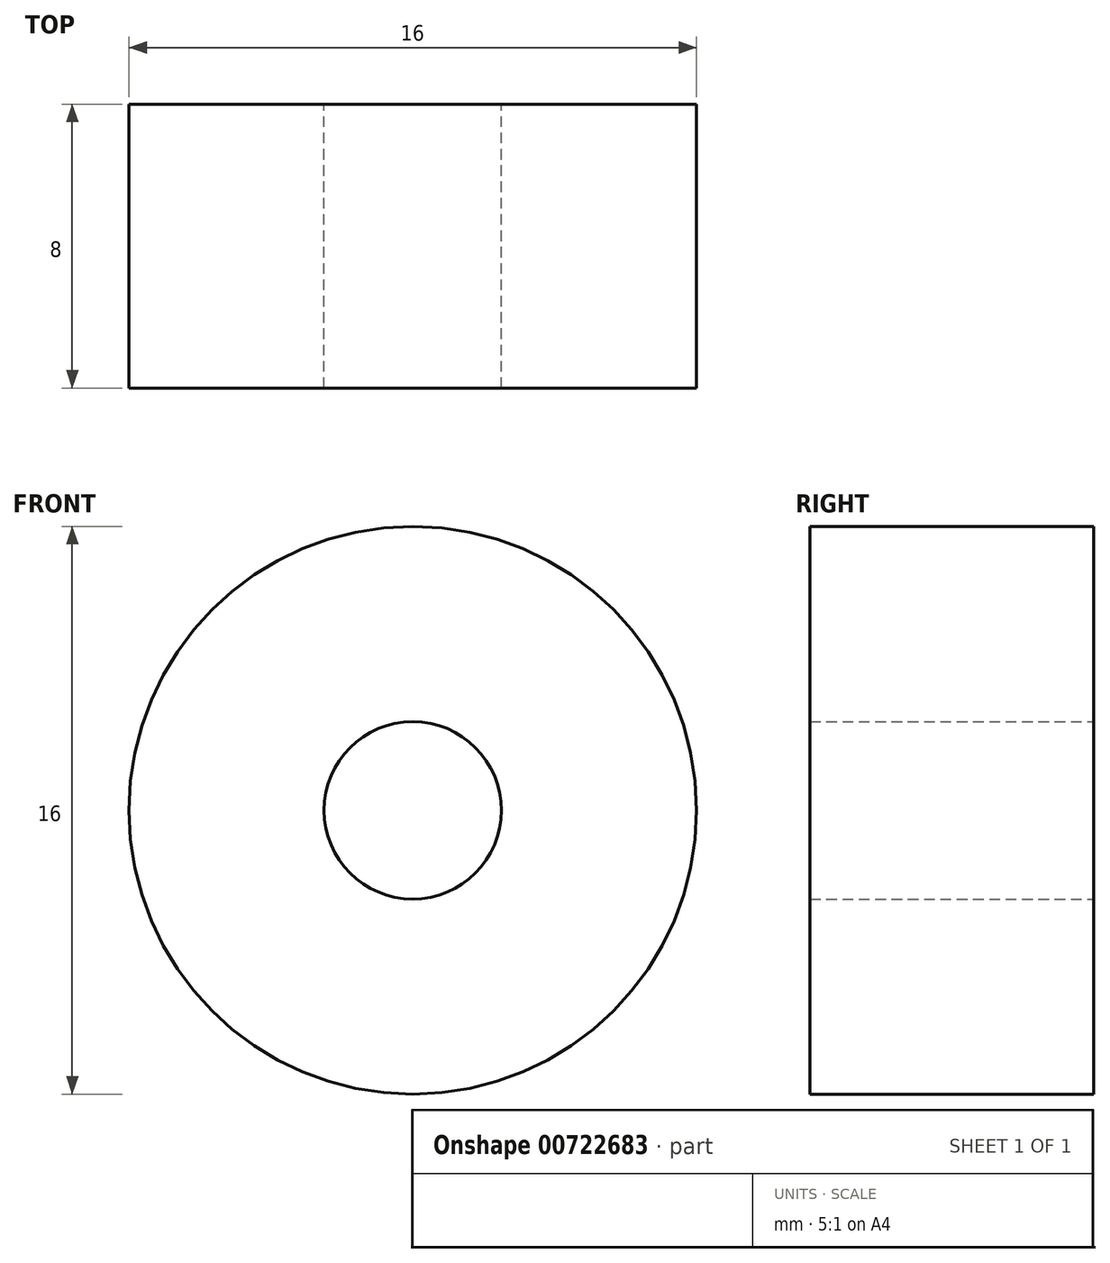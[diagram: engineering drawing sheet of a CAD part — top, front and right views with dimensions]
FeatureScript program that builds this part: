
annotation { "Feature Type Name" : "Feature", "Feature Type Description" : "" }
export const myFeature = defineFeature(function(context is Context, id is Id, definition is map)
    precondition{}
    {
        {
            var Q0;
            Q0=qCreatedBy(makeId("Front.planeOp"),FACE);
            var sketch = newSketch(context, id + "F0", { "sketchPlane" : qUnion([Q0])});
            skCircle(sketch, "E0", {"center": v(29.39, 23.18) * mm, "radius": 8 * mm});
            skCircle(sketch, "E1", {"center": v(29.39, 23.18) * mm, "radius": 2.5 * mm});
            skSolve(sketch);
        }
        {
            var Q0;
            Q0=makeQuery(id+"F0.imprint","IMPRINT",FACE,{"disambiguationData":[TD([[makeQuery(id+"F0.imprint","IMPRINT",EDGE,{"derivedFrom":sQuery(id+"F0.wireOp",EDGE,"E0")}),1.0]])]});
            extrude(context, id + "F1", {"entities" : qUnion([Q0]), "depth" : 8 * mm, "offsetDistance" : 25 * mm, "symmetric" : true});
        }
    });
